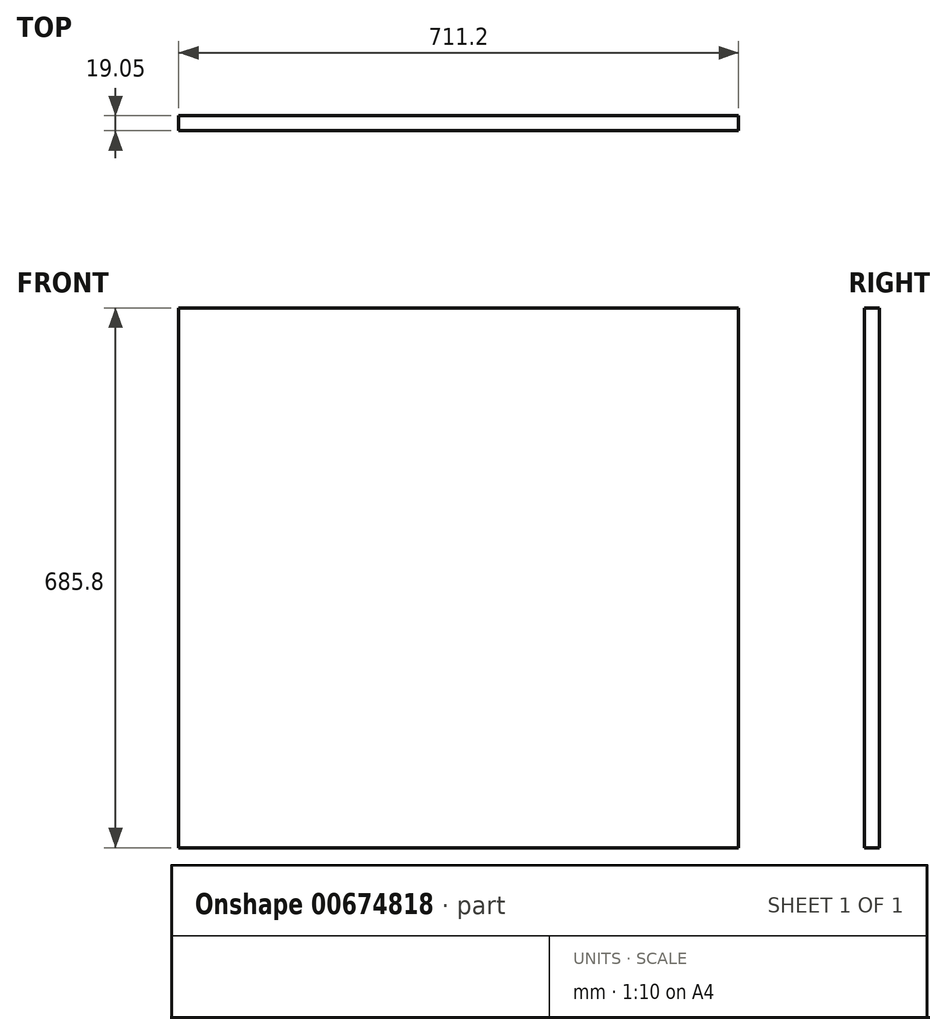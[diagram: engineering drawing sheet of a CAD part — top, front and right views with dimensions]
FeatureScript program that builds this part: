
annotation { "Feature Type Name" : "Feature", "Feature Type Description" : "" }
export const myFeature = defineFeature(function(context is Context, id is Id, definition is map)
    precondition{}
    {
        {
            var Q0;
            Q0=qCreatedBy(makeId("Front.planeOp"),FACE);
            var sketch = newSketch(context, id + "F0", { "sketchPlane" : qUnion([Q0])});
            skLineSegment(sketch, "E0.bottom", {"start": v(-355.6, 342.9) * mm, "end": v(355.6, 342.9) * mm});
            skLineSegment(sketch, "E0.top", {"start": v(-355.6, -342.9) * mm, "end": v(355.6, -342.9) * mm});
            skLineSegment(sketch, "E0.left", {"start": v(-355.6, 342.9) * mm, "end": v(-355.6, -342.9) * mm});
            skLineSegment(sketch, "E0.right", {"start": v(355.6, 342.9) * mm, "end": v(355.6, -342.9) * mm});
            skPoint(sketch, "E0.middle", {"position": v(0, 0) * mm});
            skSolve(sketch);
        }
        {
            var Q0;
            Q0=makeQuery(id+"F0.imprint","IMPRINT",FACE,{"disambiguationData":[TD([[makeQuery(id+"F0.imprint","IMPRINT",EDGE,{"derivedFrom":sQuery(id+"F0.wireOp",EDGE,"E0.bottom")}),-1.0]])]});
            extrude(context, id + "F1", {"entities" : qUnion([Q0]), "depth" : 19.05 * mm, "offsetDistance" : 25.4 * mm});
        }
    });
